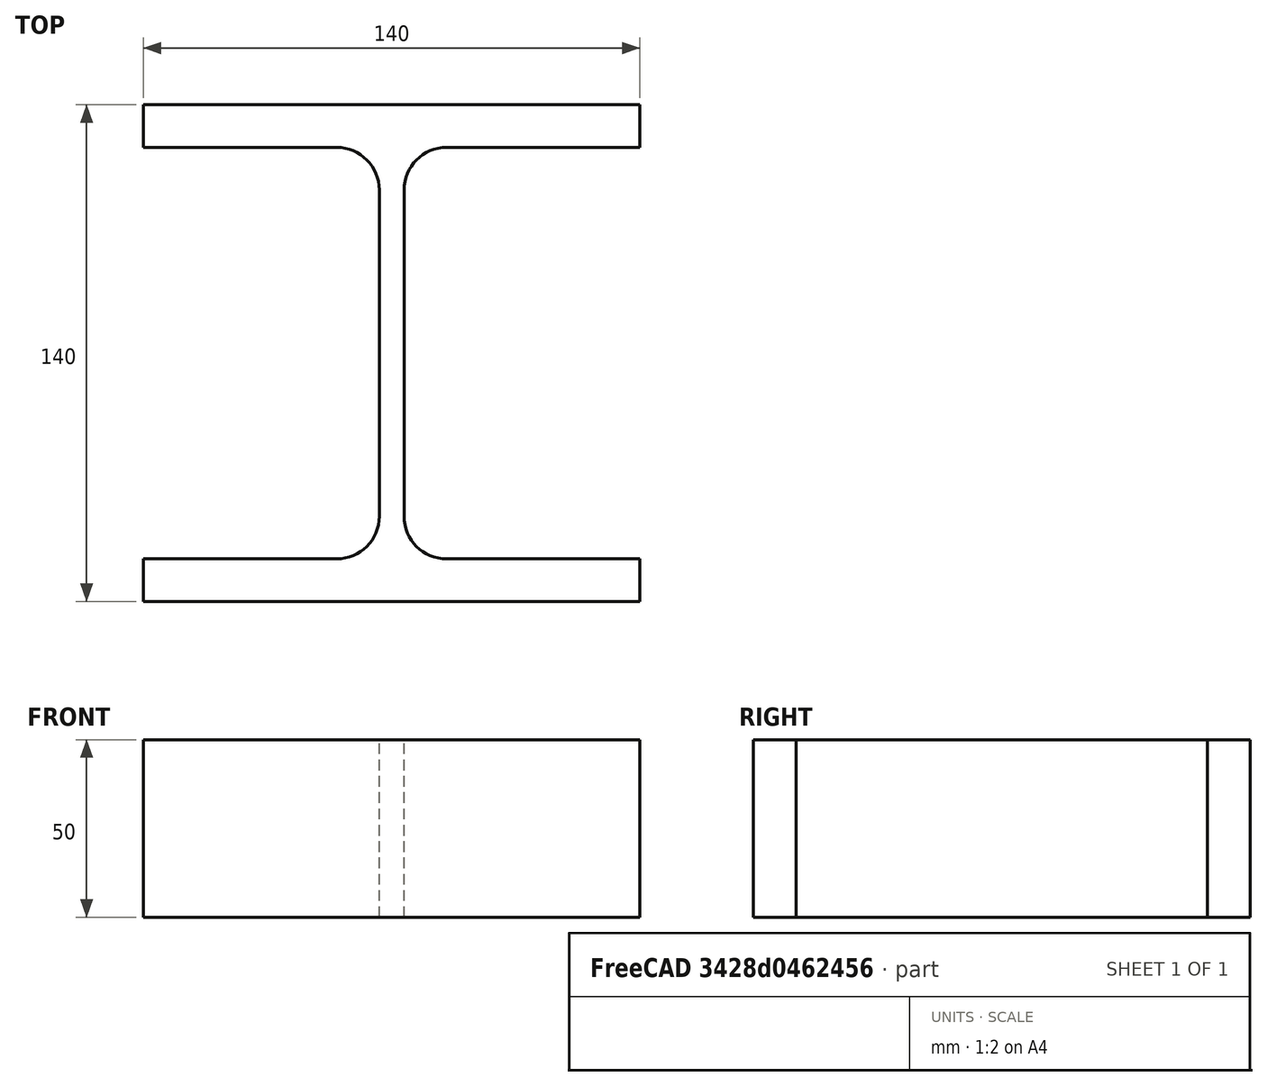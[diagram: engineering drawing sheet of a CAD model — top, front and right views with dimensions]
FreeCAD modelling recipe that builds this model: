
FCSTD DOCUMENT  (FreeCAD 0.15R4671 (Git))
Label: HE-B-Profile 140 DIN1025-2 S235JR
License: All rights reserved
LicenseURL: http://en.wikipedia.org/wiki/All_rights_reserved
objects: Sketcher::SketchObject×1, Part::Extrusion×1
note: 2 computed .brp shape members not serialized (recipe doc carries the construction recipe); baked Part::Feature solids carry a one-line shape summary decoded from their .brp

FEATURE [Sketcher::SketchObject] Sketch
  sketch-geometry (16):
    g0: LineSegment StartX=3.5 StartY=-46 StartZ=0 EndX=3.5 EndY=46 EndZ=0
    g1: LineSegment StartX=15.5 StartY=58 StartZ=0 EndX=70 EndY=58 EndZ=0
    g2: LineSegment StartX=70 StartY=58 StartZ=0 EndX=70 EndY=70 EndZ=0
    g3: LineSegment StartX=70 StartY=70 StartZ=0 EndX=-70 EndY=70 EndZ=0
    g4: LineSegment StartX=-70 StartY=70 StartZ=0 EndX=-70 EndY=58 EndZ=0
    g5: LineSegment StartX=-70 StartY=58 StartZ=0 EndX=-15.5 EndY=58 EndZ=0
    g6: LineSegment StartX=-3.5 StartY=46 StartZ=0 EndX=-3.5 EndY=-46 EndZ=0
    g7: LineSegment StartX=-15.5 StartY=-58 StartZ=0 EndX=-70 EndY=-58 EndZ=0
    g8: LineSegment StartX=-70 StartY=-58 StartZ=0 EndX=-70 EndY=-70 EndZ=0
    g9: LineSegment StartX=-70 StartY=-70 StartZ=0 EndX=70 EndY=-70 EndZ=0
    g10: LineSegment StartX=70 StartY=-70 StartZ=0 EndX=70 EndY=-58 EndZ=0
    g11: LineSegment StartX=70 StartY=-58 StartZ=0 EndX=15.5 EndY=-58 EndZ=0
    g12: ArcOfCircle CenterX=15.5 CenterY=46 CenterZ=0 NormalX=0 NormalY=0 NormalZ=1 Radius=12 StartAngle=1.5708 EndAngle=3.14159
    g13: ArcOfCircle CenterX=15.5 CenterY=-46 CenterZ=0 NormalX=0 NormalY=0 NormalZ=1 Radius=12 StartAngle=3.14159 EndAngle=4.71239
    g14: ArcOfCircle CenterX=-15.5 CenterY=46 CenterZ=0 NormalX=0 NormalY=0 NormalZ=1 Radius=12 StartAngle=0 EndAngle=1.5708
    g15: ArcOfCircle CenterX=-15.5 CenterY=-46 CenterZ=0 NormalX=0 NormalY=0 NormalZ=1 Radius=12 StartAngle=4.71239 EndAngle=6.28319
  constraints (42):
    c: Vertical(g0)
    c: Coincident(g2,g1)
    c: Vertical(g2)
    c: Coincident(g3,g2)
    c: Coincident(g4,g3)
    c: Vertical(g4)
    c: Coincident(g5,g4)
    c: Horizontal(g5)
    c: Vertical(g6)
    c: Horizontal(g7)
    c: Coincident(g8,g7)
    c: Vertical(g8)
    c: Coincident(g9,g8)
    c: Horizontal(g9)
    c: Coincident(g10,g9)
    c: Vertical(g10)
    c: Coincident(g11,g10)
    c: Horizontal(g11)
    c: Tangent(g1,g12) = 1.5708
    c: Tangent(g0,g12) = 1.5708
    c: Tangent(g0,g13) = 1.5708
    c: Tangent(g11,g13) = 1.5708
    c: Tangent(g5,g14) = 1.5708
    c: Tangent(g6,g14) = 1.5708
    c: Tangent(g6,g15) = 1.5708
    c: Tangent(g7,g15) = 1.5708
    c: Equal(g3,g9)
    c: Equal(g2,g4)
    c: Equal(g4,g8)
    c: Equal(g8,g10)
    c: Equal(g12,g14)
    c: Equal(g14,g15)
    c: Equal(g15,g13)
    c: Symmetric(g2,g3,g-2)
    c: Symmetric(g9,g8,g-2)
    c: Symmetric(g0,g6,g-2)
    c: Symmetric(g2,g9,g-1)
    c: DistanceY(g2,g9) = -140
    c: DistanceX(g3) = -140
    c: DistanceX(g0,g6) = -7
    c: DistanceY(g2) = 12
    c: Radius(g12) = 12
FEATURE [Part::Extrusion] Extrude  label="HE-B-Profile 140 DIN1025-2 S235JR"
  Base = -> Sketch
  Dir = (0,0,50)
  Solid = true
